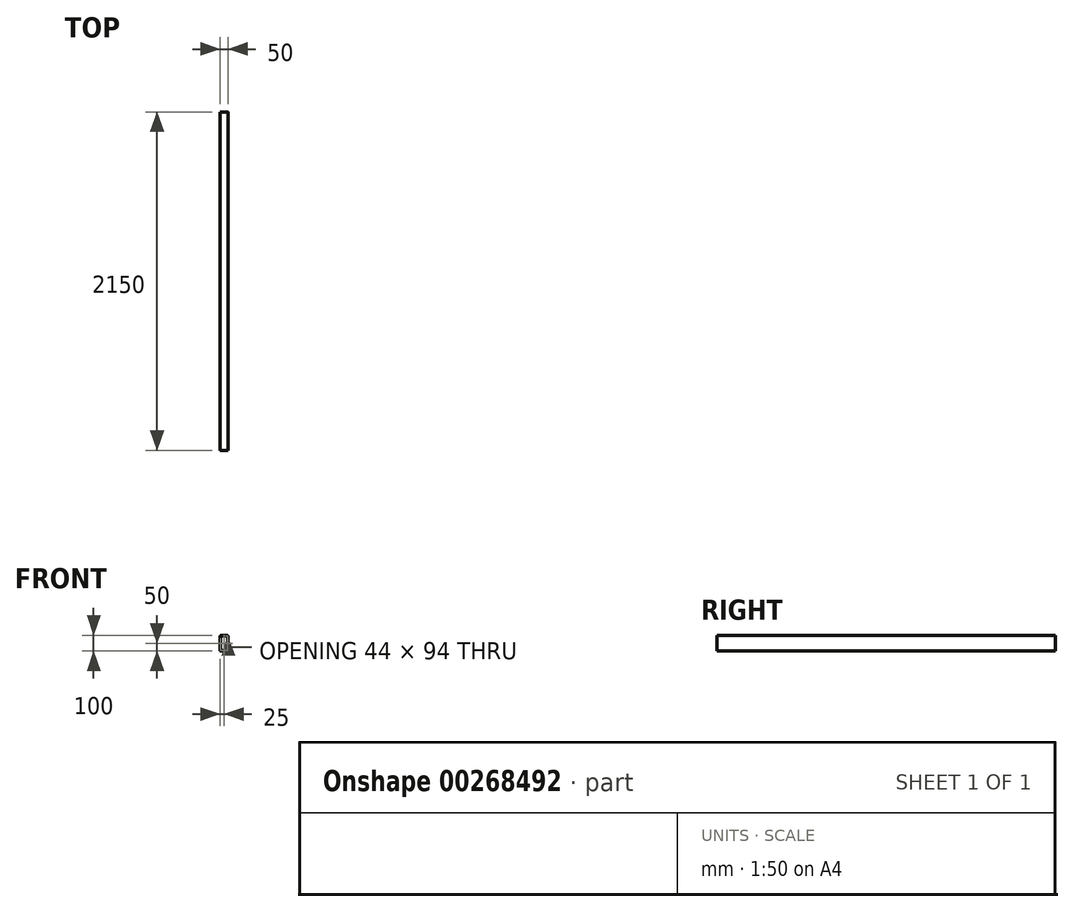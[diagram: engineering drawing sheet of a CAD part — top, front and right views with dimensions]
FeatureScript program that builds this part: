
annotation { "Feature Type Name" : "Feature", "Feature Type Description" : "" }
export const myFeature = defineFeature(function(context is Context, id is Id, definition is map)
    precondition{}
    {
        {
            var Q0;
            Q0=qCreatedBy(makeId("Front.planeOp"),FACE);
            var sketch = newSketch(context, id + "F0", { "sketchPlane" : qUnion([Q0])});
            skLineSegment(sketch, "E0", {"start": v(0, 47) * mm, "end": v(-19, 47) * mm});
            skLineSegment(sketch, "E1", {"start": v(-22, 44) * mm, "end": v(-22, -44) * mm});
            skLineSegment(sketch, "E2", {"start": v(-19, -47) * mm, "end": v(0, -47) * mm});
            skLineSegment(sketch, "E3", {"start": v(0, 50) * mm, "end": v(-19, 50) * mm});
            skLineSegment(sketch, "E4", {"start": v(-25, 44) * mm, "end": v(-25, -44) * mm});
            skLineSegment(sketch, "E5", {"start": v(-19, -50) * mm, "end": v(0, -50) * mm});
            skPoint(sketch, "E6.visualSharp", {"position": v(-22, 47) * mm});
            skArc(sketch, "E6.filletArc", {"start": v(-19, 47) * mm, "mid": v(-21.12, 46.12) * mm, "end": v(-22, 44) * mm});
            skPoint(sketch, "E7.visualSharp", {"position": v(-22, -47) * mm});
            skArc(sketch, "E7.filletArc", {"start": v(-22, -44) * mm, "mid": v(-21.12, -46.12) * mm, "end": v(-19, -47) * mm});
            skPoint(sketch, "E8.visualSharp", {"position": v(-25, 50) * mm});
            skArc(sketch, "E8.filletArc", {"start": v(-19, 50) * mm, "mid": v(-23.24, 48.24) * mm, "end": v(-25, 44) * mm});
            skPoint(sketch, "E9.visualSharp", {"position": v(-25, -50) * mm});
            skArc(sketch, "E9.filletArc", {"start": v(-25, -44) * mm, "mid": v(-23.24, -48.24) * mm, "end": v(-19, -50) * mm});
            skArc(sketch, "E10.MirrorCS", {"start": v(19, 47) * mm, "mid": v(21.12, 46.12) * mm, "end": v(22, 44) * mm});
            skArc(sketch, "E11.MirrorCS", {"start": v(22, -44) * mm, "mid": v(21.12, -46.12) * mm, "end": v(19, -47) * mm});
            skArc(sketch, "E12.MirrorCS", {"start": v(19, 50) * mm, "mid": v(23.24, 48.24) * mm, "end": v(25, 44) * mm});
            skArc(sketch, "E13.MirrorCS", {"start": v(25, -44) * mm, "mid": v(23.24, -48.24) * mm, "end": v(19, -50) * mm});
            skPoint(sketch, "E14.MirrorP", {"position": v(25, 50) * mm});
            skPoint(sketch, "E15.MirrorP", {"position": v(25, -50) * mm});
            skLineSegment(sketch, "E16.MirrorCS", {"start": v(0, 47) * mm, "end": v(19, 47) * mm});
            skPoint(sketch, "E17.MirrorP", {"position": v(22, -47) * mm});
            skLineSegment(sketch, "E18.MirrorCS", {"start": v(22, 44) * mm, "end": v(22, -44) * mm});
            skLineSegment(sketch, "E19.MirrorCS", {"start": v(19, -47) * mm, "end": v(0, -47) * mm});
            skPoint(sketch, "E20.MirrorP", {"position": v(22, 47) * mm});
            skLineSegment(sketch, "E21.MirrorCS", {"start": v(19, -50) * mm, "end": v(0, -50) * mm});
            skLineSegment(sketch, "E22.MirrorCS", {"start": v(0, 50) * mm, "end": v(19, 50) * mm});
            skLineSegment(sketch, "E23.MirrorCS", {"start": v(25, 44) * mm, "end": v(25, -44) * mm});
            skSolve(sketch);
        }
        {
            var Q0;
            Q0 = qSketchRegion(id + "F0", true);
            extrude(context, id + "F1", {"entities" : qUnion([Q0]), "depth" : 2150 * mm});
        }
    });
